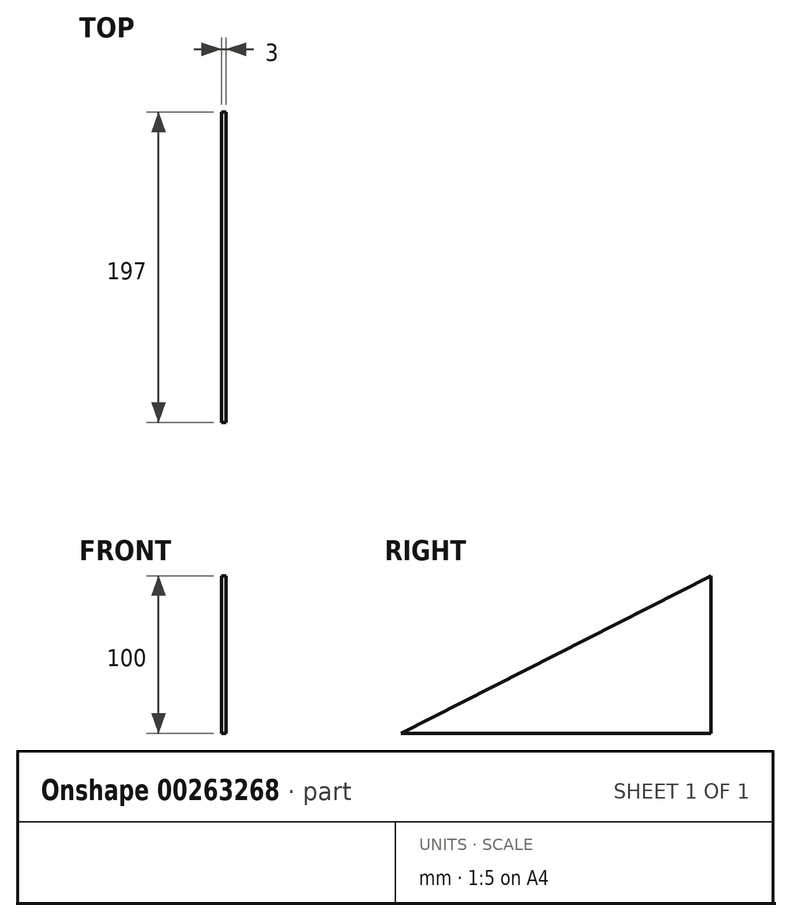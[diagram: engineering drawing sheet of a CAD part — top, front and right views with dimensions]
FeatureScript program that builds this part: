
annotation { "Feature Type Name" : "Feature", "Feature Type Description" : "" }
export const myFeature = defineFeature(function(context is Context, id is Id, definition is map)
    precondition{}
    {
        {
            var Q0;
            Q0=qCreatedBy(makeId("Right.planeOp"),FACE);
            var sketch = newSketch(context, id + "F0", { "sketchPlane" : qUnion([Q0])});
            skLineSegment(sketch, "E0", {"start": v(0, 0) * mm, "end": v(-197, 0) * mm});
            skLineSegment(sketch, "E1", {"start": v(-197, 0) * mm, "end": v(0, 100) * mm});
            skLineSegment(sketch, "E2", {"start": v(0, 100) * mm, "end": v(0, 0) * mm});
            skSolve(sketch);
        }
        {
            var Q0;
            Q0 = qSketchRegion(id + "F0", true);
            extrude(context, id + "F1", {"entities" : qUnion([Q0]), "depth" : 3 * mm});
        }
    });
